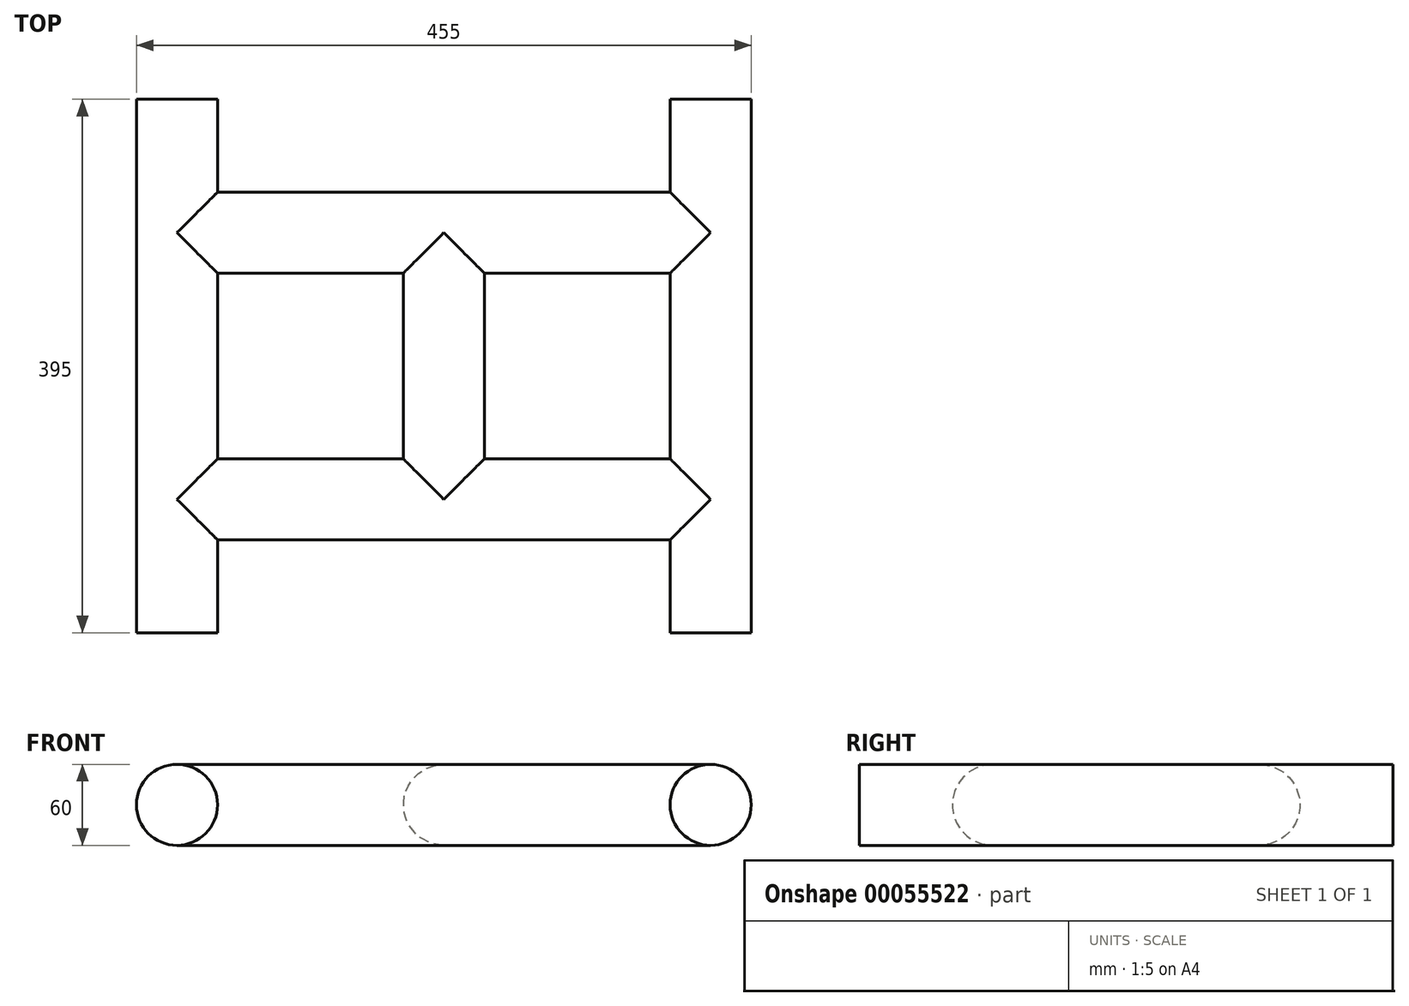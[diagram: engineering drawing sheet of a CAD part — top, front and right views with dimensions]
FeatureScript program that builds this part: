
annotation { "Feature Type Name" : "Feature", "Feature Type Description" : "" }
export const myFeature = defineFeature(function(context is Context, id is Id, definition is map)
    precondition{}
    {
        {
            var Q0;
            Q0=qCreatedBy(makeId("Front.planeOp"),FACE);
            var sketch = newSketch(context, id + "F0", { "sketchPlane" : qUnion([Q0])});
            skCircle(sketch, "E0", {"center": v(0, 0) * mm, "radius": 30 * mm});
            skPoint(sketch, "E1", {"position": v(197.5, 0) * mm});
            skCircle(sketch, "E2", {"center": v(197.5, 0) * mm, "radius": 30 * mm});
            skSolve(sketch);
        }
        {
            var Q0;
            Q0=makeQuery(id+"F0.imprint","IMPRINT",FACE,{"disambiguationData":[TD([[makeQuery(id+"F0.imprint","IMPRINT",EDGE,{"derivedFrom":sQuery(id+"F0.wireOp",EDGE,"E0")}),1.0]])]});
            extrude(context, id + "F1", {"entities" : qUnion([Q0]), "endBound" : BoundingType.SYMMETRIC, "depth" : 395 * mm});
        }
        {
            var Q0;
            Q0=makeQuery(id+"F0.imprint","IMPRINT",FACE,{"disambiguationData":[TD([[makeQuery(id+"F0.imprint","IMPRINT",EDGE,{"derivedFrom":sQuery(id+"F0.wireOp",EDGE,"E2")}),1.0]])]});
            extrude(context, id + "F2", {"entities" : qUnion([Q0]), "endBound" : BoundingType.SYMMETRIC, "depth" : (395 / 2) * mm});
        }
        {
            var Q0;
            Q0=qCreatedBy(makeId("Right.planeOp"),FACE);
            var Q1;
            Q1=sQuery(id+"F0.wireOp",VERTEX,"E1");
            cPlane(context, id + "F3", {"entities" : qUnion([Q0, Q1]), "cplaneType" : CPlaneType.PLANE_POINT, "offset" : 150 * mm, "width" : 150 * mm, "height" : 150 * mm});
        }
        {
            var Q0;
            Q0=makeQuery(id+"F1.opExtrude","SWEPT_BODY",BODY,{"disambiguationData":[OSD([sQuery(id+"F0.wireOp",EDGE,"E0")])]});
            var Q1;
            Q1=qCreatedBy(id+"F3.planeOp",FACE);
            mirror(context, id + "F4", {"entities" : qUnion([Q0]), "mirrorPlane" : qUnion([Q1])});
        }
        {
            var Q0;
            Q0=qCreatedBy(id+"F3.planeOp",FACE);
            var sketch = newSketch(context, id + "F5", { "sketchPlane" : qUnion([Q0])});
            skPoint(sketch, "E3", {"position": v(0, 0) * mm});
            skPoint(sketch, "E4", {"position": v(-98.75, 0) * mm});
            skPoint(sketch, "E5", {"position": v(98.75, 0) * mm});
            skCircle(sketch, "E6", {"center": v(-98.75, 0) * mm, "radius": 30 * mm});
            skCircle(sketch, "E7", {"center": v(98.75, 0) * mm, "radius": 30 * mm});
            skSolve(sketch);
        }
        {
            var Q0;
            Q0 = qSketchRegion(id + "F5", true);
            extrude(context, id + "F6", {"entities" : qUnion([Q0]), "operationType" : NewBodyOperationType.ADD, "endBound" : BoundingType.SYMMETRIC, "depth" : 395 * mm});
        }
    });
